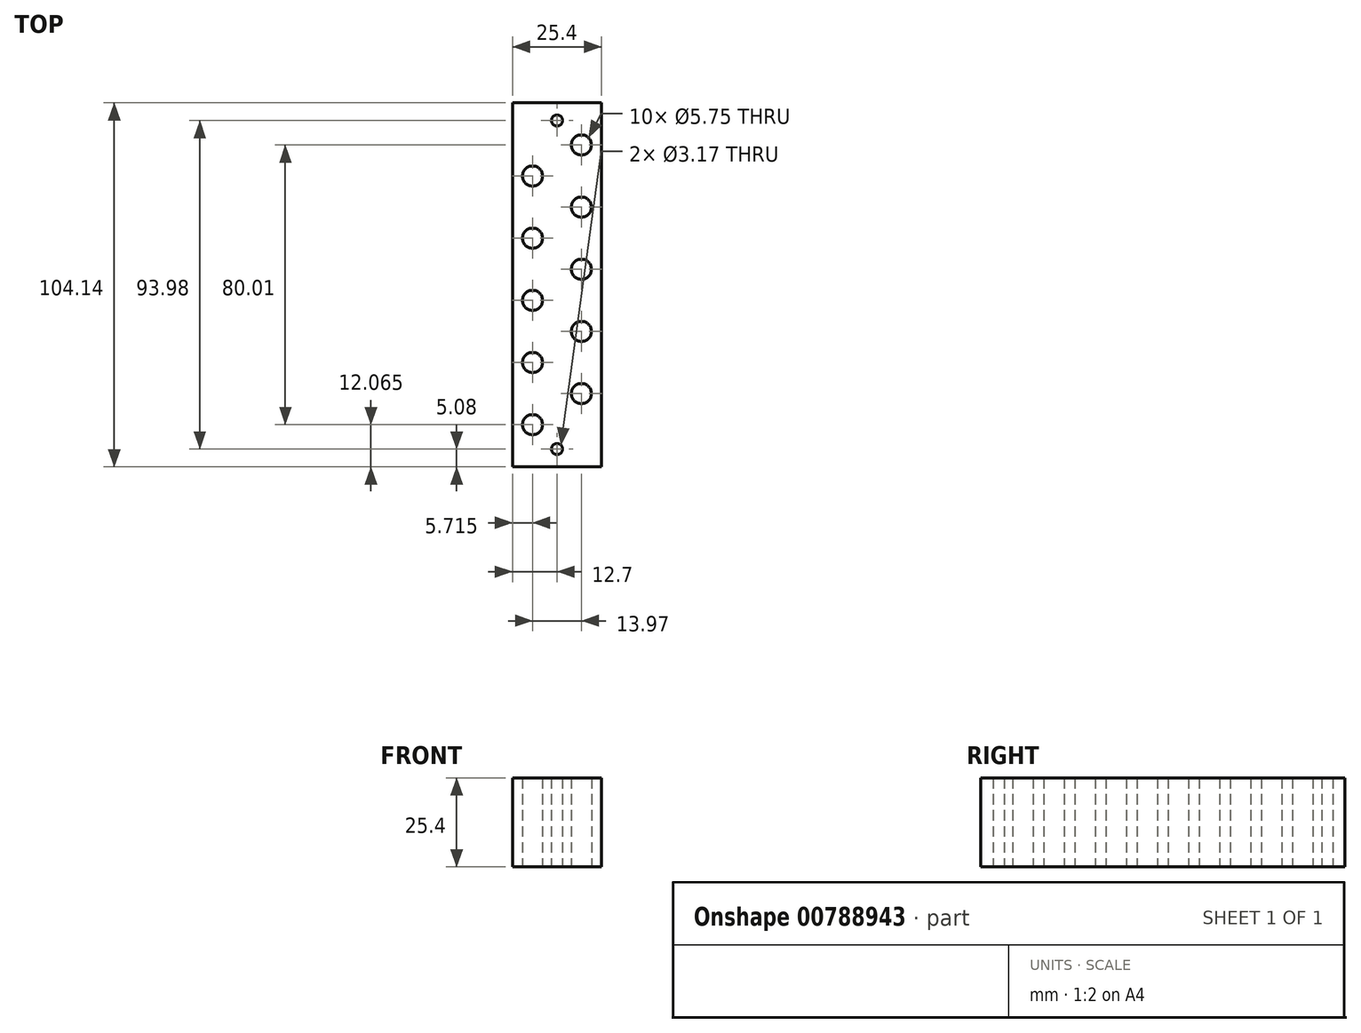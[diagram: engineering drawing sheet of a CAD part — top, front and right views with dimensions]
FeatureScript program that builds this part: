
annotation { "Feature Type Name" : "Feature", "Feature Type Description" : "" }
export const myFeature = defineFeature(function(context is Context, id is Id, definition is map)
    precondition{}
    {
        {
            var Q0;
            Q0=qCreatedBy(makeId("Top.planeOp"),FACE);
            var sketch = newSketch(context, id + "F0", { "sketchPlane" : qUnion([Q0])});
            skLineSegment(sketch, "E0.bottom", {"start": v(0, 0) * mm, "end": v(25.4, 0) * mm});
            skLineSegment(sketch, "E0.top", {"start": v(0, 104.14) * mm, "end": v(25.4, 104.14) * mm});
            skLineSegment(sketch, "E0.left", {"start": v(0, 0) * mm, "end": v(0, 104.14) * mm});
            skLineSegment(sketch, "E0.right", {"start": v(25.4, 0) * mm, "end": v(25.4, 104.14) * mm});
            skCircle(sketch, "E1", {"center": v(12.7, 5.08) * mm, "radius": 1.59 * mm});
            skPoint(sketch, "E2", {"position": v(12.7, 0) * mm});
            skCircle(sketch, "E3", {"center": v(12.7, 99.06) * mm, "radius": 1.59 * mm});
            skLineSegment(sketch, "E4", {"start": v(12.7, 5.08) * mm, "end": v(12.7, 99.06) * mm});
            skPoint(sketch, "E5", {"position": v(12.7, 52.07) * mm});
            skPoint(sketch, "E6", {"position": v(0, 52.07) * mm});
            skCircle(sketch, "E7", {"center": v(5.72, 47.62) * mm, "radius": 2.88 * mm});
            skCircle(sketch, "E8", {"center": v(19.69, 56.51) * mm, "radius": 2.88 * mm});
            skLineSegment(sketch, "E9", {"start": v(5.72, 47.62) * mm, "end": v(19.69, 56.51) * mm});
            skCircle(sketch, "E10.1.0.0", {"center": v(19.69, 74.3) * mm, "radius": 2.88 * mm});
            skCircle(sketch, "E10.1.0.1", {"center": v(5.72, 65.4) * mm, "radius": 2.88 * mm});
            skCircle(sketch, "E10.2.0.0", {"center": v(19.69, 92.07) * mm, "radius": 2.88 * mm});
            skCircle(sketch, "E10.2.0.1", {"center": v(5.72, 83.19) * mm, "radius": 2.88 * mm});
            skLineSegment(sketch, "E10.direction1", {"start": v(19.69, 56.51) * mm, "end": v(19.69, 74.3) * mm, "construction": true});
            skLineSegment(sketch, "E11", {"start": v(-0.81, 52.07) * mm, "end": v(12.7, 52.07) * mm});
            skCircle(sketch, "E12.1.0.0", {"center": v(5.72, 29.84) * mm, "radius": 2.88 * mm});
            skCircle(sketch, "E12.1.0.1", {"center": v(19.69, 38.73) * mm, "radius": 2.88 * mm});
            skCircle(sketch, "E12.2.0.0", {"center": v(5.72, 12.06) * mm, "radius": 2.88 * mm});
            skCircle(sketch, "E12.2.0.1", {"center": v(19.69, 20.95) * mm, "radius": 2.88 * mm});
            skLineSegment(sketch, "E12.direction1", {"start": v(5.72, 47.62) * mm, "end": v(5.72, 29.84) * mm, "construction": true});
            skLineSegment(sketch, "E13", {"start": v(5.72, 65.4) * mm, "end": v(19.69, 56.51) * mm});
            skSolve(sketch);
        }
        {
            var Q0;
            {var subQ8=sQuery(id+"F0.wireOp",EDGE,"E0.bottom");Q0=makeQuery(id+"F0.imprint","IMPRINT",FACE,{"disambiguationData":[TD([[makeQuery(id+"F0.imprint","IMPRINT",EDGE,{"derivedFrom":subQ8}),1.0]])]});}
            var Q1;
            {var subQ0=sQuery(id+"F0.wireOp",EDGE,"E9");var subQ1=sQuery(id+"F0.wireOp",EDGE,"E4");var subQ2=makeQuery(id+"F0.imprint","INTERSECT",VERTEX,{"derivedFrom":[subQ1,subQ0]});Q1=makeQuery(id+"F0.imprint","IMPRINT",FACE,{"disambiguationData":[TD([[makeQuery(id+"F0.imprint","IMPRINT",EDGE,{"disambiguationData":[TD([[subQ2,-1.0]])],"derivedFrom":subQ1}),-1.0]])]});}
            extrude(context, id + "F1", {"entities" : qUnion([Q0, Q1]), "depth" : 25.4 * mm, "offsetDistance" : 25.4 * mm});
        }
    });
